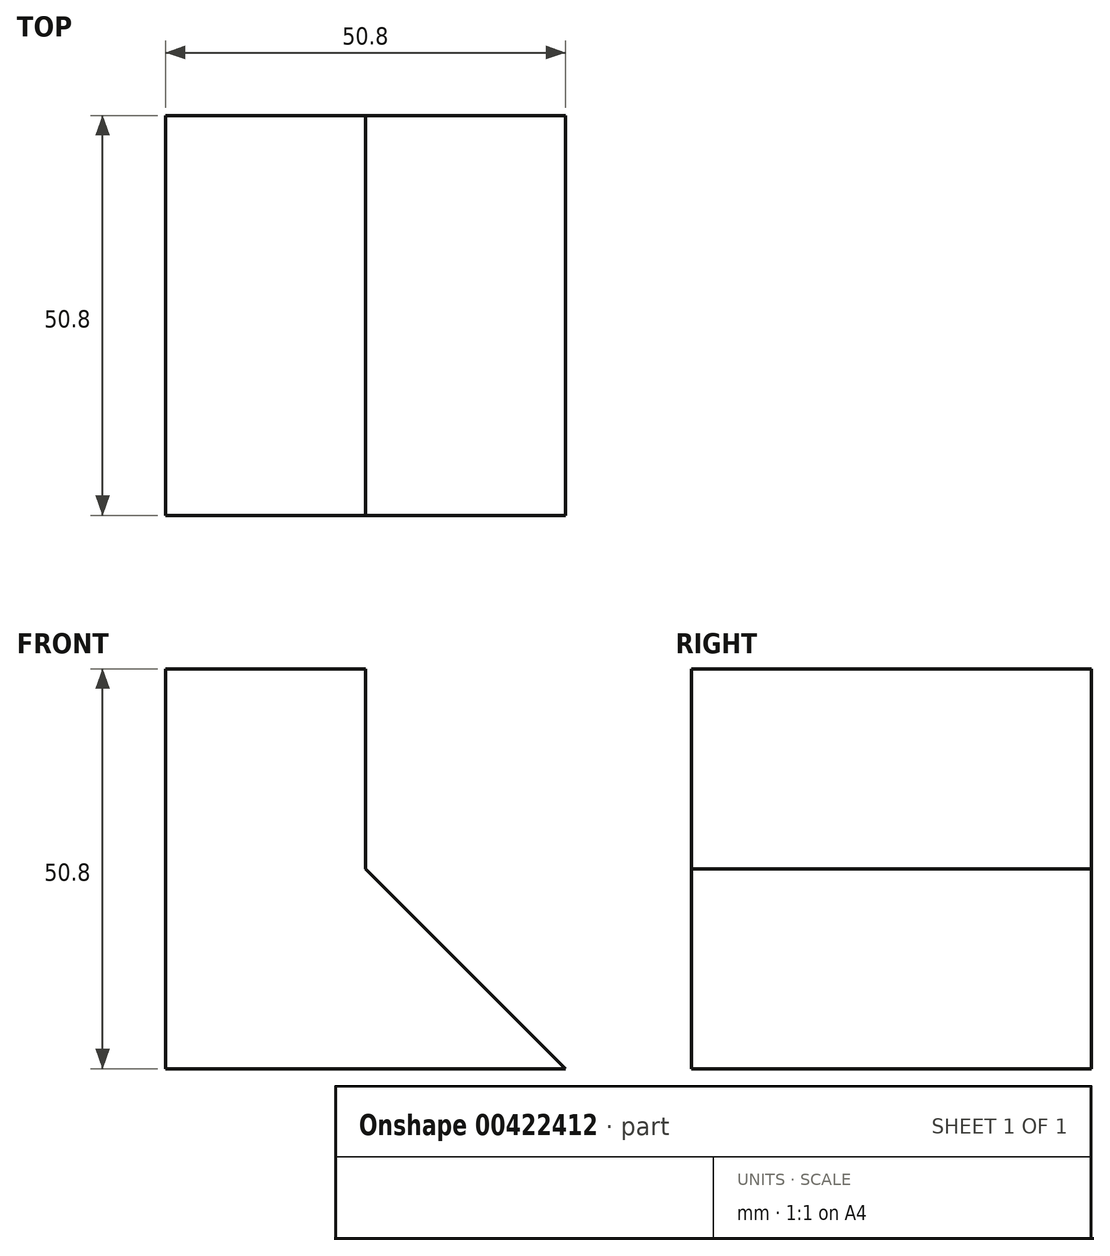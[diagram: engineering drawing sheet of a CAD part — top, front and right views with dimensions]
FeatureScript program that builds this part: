
annotation { "Feature Type Name" : "Feature", "Feature Type Description" : "" }
export const myFeature = defineFeature(function(context is Context, id is Id, definition is map)
    precondition{}
    {
        {
            var Q0;
            Q0=qCreatedBy(makeId("Front.planeOp"),FACE);
            var sketch = newSketch(context, id + "F0", { "sketchPlane" : qUnion([Q0])});
            skLineSegment(sketch, "E0", {"start": v(-50.8, 50.8) * mm, "end": v(-50.8, 0) * mm});
            skLineSegment(sketch, "E1", {"start": v(-50.8, 0) * mm, "end": v(0, 0) * mm});
            skLineSegment(sketch, "E2", {"start": v(0, 0) * mm, "end": v(-50.8, 0) * mm});
            skLineSegment(sketch, "E3", {"start": v(-50.8, 50.8) * mm, "end": v(-25.4, 50.8) * mm});
            skLineSegment(sketch, "E4", {"start": v(-25.4, 50.8) * mm, "end": v(-25.4, 25.4) * mm});
            skLineSegment(sketch, "E5", {"start": v(-25.4, 25.4) * mm, "end": v(0, 0) * mm});
            skSolve(sketch);
        }
        {
            var Q0;
            Q0 = qSketchRegion(id + "F0", true);
            extrude(context, id + "F1", {"entities" : qUnion([Q0]), "depth" : 50.8 * mm});
        }
    });
